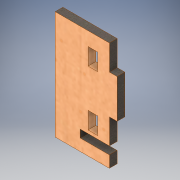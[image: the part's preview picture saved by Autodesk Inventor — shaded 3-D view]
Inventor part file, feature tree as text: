
AUTODESK INVENTOR PART (.ipt)
format: ipt  version: 2019 (Build 230136000, 136)  size: 140,800 bytes
history: native  units: mm
features: other x1, extrude x1, sketch x1
ambient origin geometry x8: Origin, YZ Plane, XZ Plane, XY Plane, X Axis, Y Axis, Z Axis, Center Point
bodies: Body1 (feature_tree)
feature tree (3):
  other  "Твердое тело1"
  extrude  "Выдавливание1"  Depth=4.0mm
  sketch  "Эскиз1"
